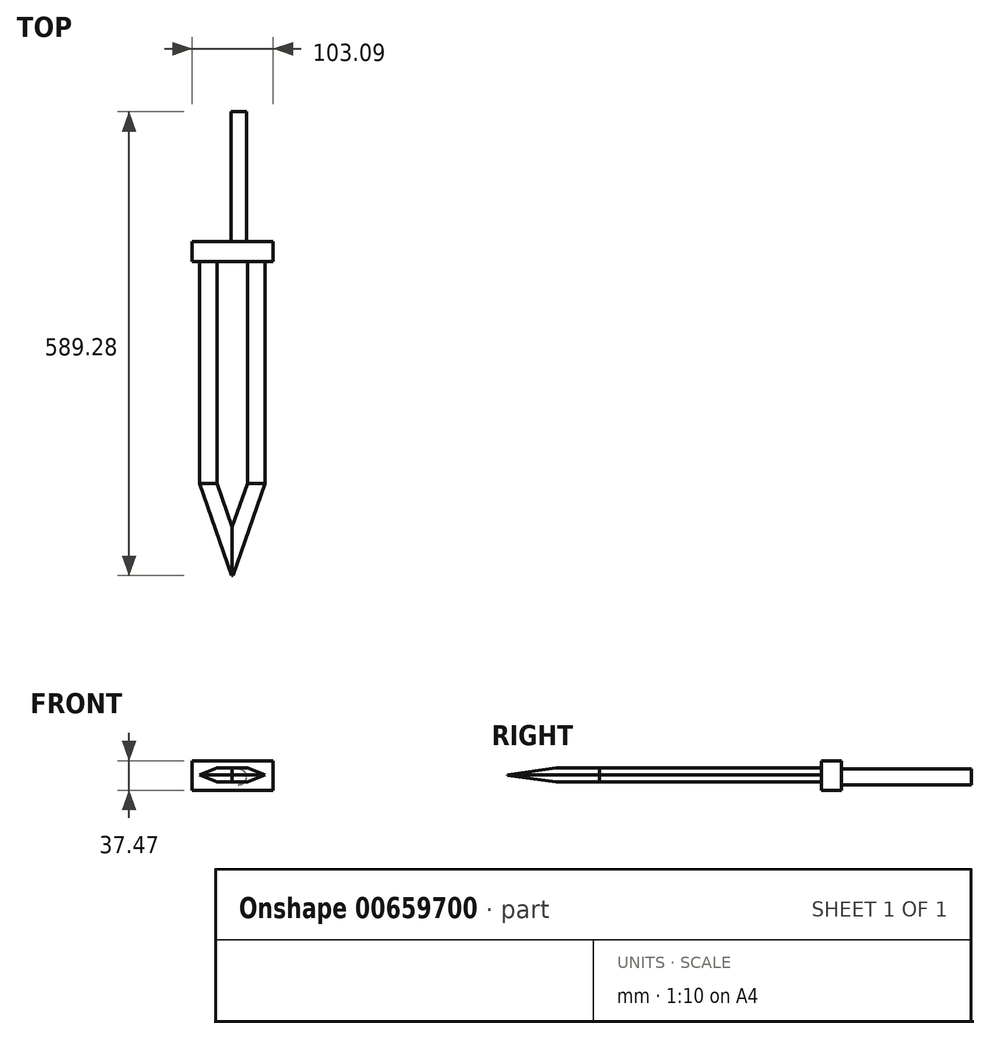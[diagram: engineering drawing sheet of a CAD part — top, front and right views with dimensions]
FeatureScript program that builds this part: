
annotation { "Feature Type Name" : "Feature", "Feature Type Description" : "" }
export const myFeature = defineFeature(function(context is Context, id is Id, definition is map)
    precondition{}
    {
        {
            var Q0;
            Q0=qCreatedBy(makeId("Front.planeOp"),FACE);
            var sketch = newSketch(context, id + "F0", { "sketchPlane" : qUnion([Q0])});
            skLineSegment(sketch, "E0.bottom", {"start": v(-59.18, 20.63) * mm, "end": v(43.91, 20.63) * mm});
            skLineSegment(sketch, "E0.top", {"start": v(-59.18, -16.84) * mm, "end": v(43.91, -16.84) * mm});
            skLineSegment(sketch, "E0.left", {"start": v(-59.18, 20.63) * mm, "end": v(-59.18, -16.84) * mm});
            skLineSegment(sketch, "E0.right", {"start": v(43.91, 20.63) * mm, "end": v(43.91, -16.84) * mm});
            skSolve(sketch);
        }
        {
            var Q0;
            Q0 = qSketchRegion(id + "F0", true);
            extrude(context, id + "F1", {"entities" : qUnion([Q0]), "depth" : 25.4 * mm, "offsetDistance" : 25.4 * mm});
        }
        {
            var Q0;
            Q0=makeQuery(id+"F1.opExtrude","CAP_FACE",FACE,{"disambiguationData":[OSD([sQuery(id+"F0.wireOp",EDGE,"E0.bottom"),sQuery(id+"F0.wireOp",EDGE,"E0.top"),sQuery(id+"F0.wireOp",EDGE,"E0.left"),sQuery(id+"F0.wireOp",EDGE,"E0.right")])],"isStart":true});
            var sketch = newSketch(context, id + "F2", { "sketchPlane" : qUnion([Q0])});
            skCircle(sketch, "E1", {"center": v(0, 0) * mm, "radius": 9.89 * mm});
            skSolve(sketch);
        }
        {
            var Q0;
            Q0 = qSketchRegion(id + "F2", true);
            extrude(context, id + "F3", {"entities" : qUnion([Q0]), "operationType" : NewBodyOperationType.ADD, "depth" : 165.1 * mm, "offsetDistance" : 25.4 * mm});
        }
        {
            var Q0;
            Q0=makeQuery(id+"F1.opExtrude","CAP_FACE",FACE,{"disambiguationData":[OSD([sQuery(id+"F0.wireOp",EDGE,"E0.bottom"),sQuery(id+"F0.wireOp",EDGE,"E0.top"),sQuery(id+"F0.wireOp",EDGE,"E0.left"),sQuery(id+"F0.wireOp",EDGE,"E0.right")])],"isStart":false});
            var sketch = newSketch(context, id + "F4", { "sketchPlane" : qUnion([Q0])});
            skLineSegment(sketch, "E2.bottom", {"start": v(-52.94, 11.26) * mm, "end": v(36.6, 11.26) * mm});
            skLineSegment(sketch, "E2.top", {"start": v(-52.94, -6.61) * mm, "end": v(36.6, -6.61) * mm});
            skLineSegment(sketch, "E2.left", {"start": v(-52.94, 11.26) * mm, "end": v(-52.94, -6.61) * mm});
            skLineSegment(sketch, "E2.right", {"start": v(36.6, 11.26) * mm, "end": v(36.6, -6.61) * mm});
            skSolve(sketch);
        }
        {
            var Q0;
            Q0 = qSketchRegion(id + "F4", true);
            extrude(context, id + "F5", {"entities" : qUnion([Q0]), "operationType" : NewBodyOperationType.ADD, "depth" : 398.78 * mm, "offsetDistance" : 25.4 * mm});
        }
        {
            var Q0;
            Q0=makeQuery(id+"F5.opExtrude","SWEPT_EDGE",EDGE,{"disambiguationData":[OSD([sQuery(id+"F4.wireOp",EDGE,"E2.top"),sQuery(id+"F4.wireOp",EDGE,"E2.left")])]});
            var Q1;
            Q1=makeQuery(id+"F5.opExtrude","SWEPT_EDGE",EDGE,{"disambiguationData":[OSD([sQuery(id+"F4.wireOp",EDGE,"E2.bottom"),sQuery(id+"F4.wireOp",EDGE,"E2.left")])]});
            var Q2;
            Q2=makeQuery(id+"F5.opExtrude","SWEPT_EDGE",EDGE,{"disambiguationData":[OSD([sQuery(id+"F4.wireOp",EDGE,"E2.top"),sQuery(id+"F4.wireOp",EDGE,"E2.right")])]});
            var Q3;
            Q3=makeQuery(id+"F5.opExtrude","SWEPT_EDGE",EDGE,{"disambiguationData":[OSD([sQuery(id+"F4.wireOp",EDGE,"E2.bottom"),sQuery(id+"F4.wireOp",EDGE,"E2.right")])]});
            chamfer(context, id + "F6", {"entities" : qUnion([Q0, Q1, Q2, Q3]), "chamferType" : ChamferType.TWO_OFFSETS, "width1" : 25.4 * mm, "oppositeDirection" : false, "width2" : 10.16 * mm, "tangentPropagation" : true});
        }
        {
            var Q0;
            {var subQ0=sQuery(id+"F4.wireOp",EDGE,"E2.left");var subQ1=sQuery(id+"F4.wireOp",EDGE,"E2.top");Q0=makeQuery(id+"F6.opChamfer","BLEND_EDGE",EDGE,{"blendedFrom":[makeQuery(id+"F5.opExtrude","SWEPT_EDGE",EDGE,{"disambiguationData":[OSD([subQ1,subQ0])]}),makeQuery(id+"F5.opExtrude","CAP_FACE",FACE,{"disambiguationData":[OSD([sQuery(id+"F4.wireOp",EDGE,"E2.bottom"),subQ1,subQ0,sQuery(id+"F4.wireOp",EDGE,"E2.right")])],"isStart":false})],"blendedInto":[makeQuery(id+"F5.opExtrude","CAP_FACE",FACE,{"disambiguationData":[OSD([sQuery(id+"F4.wireOp",EDGE,"E2.bottom"),subQ1,subQ0,sQuery(id+"F4.wireOp",EDGE,"E2.right")])],"isStart":false})]});}
            var Q1;
            {var subQ0=sQuery(id+"F4.wireOp",EDGE,"E2.left");var subQ1=sQuery(id+"F4.wireOp",EDGE,"E2.bottom");Q1=makeQuery(id+"F6.opChamfer","BLEND_EDGE",EDGE,{"blendedFrom":[makeQuery(id+"F5.opExtrude","SWEPT_EDGE",EDGE,{"disambiguationData":[OSD([subQ1,subQ0])]}),makeQuery(id+"F5.opExtrude","CAP_FACE",FACE,{"disambiguationData":[OSD([subQ1,sQuery(id+"F4.wireOp",EDGE,"E2.top"),subQ0,sQuery(id+"F4.wireOp",EDGE,"E2.right")])],"isStart":false})],"blendedInto":[makeQuery(id+"F5.opExtrude","CAP_FACE",FACE,{"disambiguationData":[OSD([subQ1,sQuery(id+"F4.wireOp",EDGE,"E2.top"),subQ0,sQuery(id+"F4.wireOp",EDGE,"E2.right")])],"isStart":false})]});}
            var Q2;
            {var subQ0=sQuery(id+"F4.wireOp",EDGE,"E2.right");var subQ1=sQuery(id+"F4.wireOp",EDGE,"E2.top");Q2=makeQuery(id+"F6.opChamfer","BLEND_EDGE",EDGE,{"blendedFrom":[makeQuery(id+"F5.opExtrude","SWEPT_EDGE",EDGE,{"disambiguationData":[OSD([subQ1,subQ0])]}),makeQuery(id+"F5.opExtrude","CAP_FACE",FACE,{"disambiguationData":[OSD([sQuery(id+"F4.wireOp",EDGE,"E2.bottom"),subQ1,sQuery(id+"F4.wireOp",EDGE,"E2.left"),subQ0])],"isStart":false})],"blendedInto":[makeQuery(id+"F5.opExtrude","CAP_FACE",FACE,{"disambiguationData":[OSD([sQuery(id+"F4.wireOp",EDGE,"E2.bottom"),subQ1,sQuery(id+"F4.wireOp",EDGE,"E2.left"),subQ0])],"isStart":false})]});}
            var Q3;
            {var subQ0=sQuery(id+"F4.wireOp",EDGE,"E2.right");var subQ1=sQuery(id+"F4.wireOp",EDGE,"E2.bottom");Q3=makeQuery(id+"F6.opChamfer","BLEND_EDGE",EDGE,{"blendedFrom":[makeQuery(id+"F5.opExtrude","SWEPT_EDGE",EDGE,{"disambiguationData":[OSD([subQ1,subQ0])]}),makeQuery(id+"F5.opExtrude","CAP_FACE",FACE,{"disambiguationData":[OSD([subQ1,sQuery(id+"F4.wireOp",EDGE,"E2.top"),sQuery(id+"F4.wireOp",EDGE,"E2.left"),subQ0])],"isStart":false})],"blendedInto":[makeQuery(id+"F5.opExtrude","CAP_FACE",FACE,{"disambiguationData":[OSD([subQ1,sQuery(id+"F4.wireOp",EDGE,"E2.top"),sQuery(id+"F4.wireOp",EDGE,"E2.left"),subQ0])],"isStart":false})]});}
            chamfer(context, id + "F7", {"entities" : qUnion([Q0, Q1, Q2, Q3]), "chamferType" : ChamferType.TWO_OFFSETS, "width1" : 15.24 * mm, "oppositeDirection" : false, "width2" : 116.84 * mm, "tangentPropagation" : true});
        }
    });
